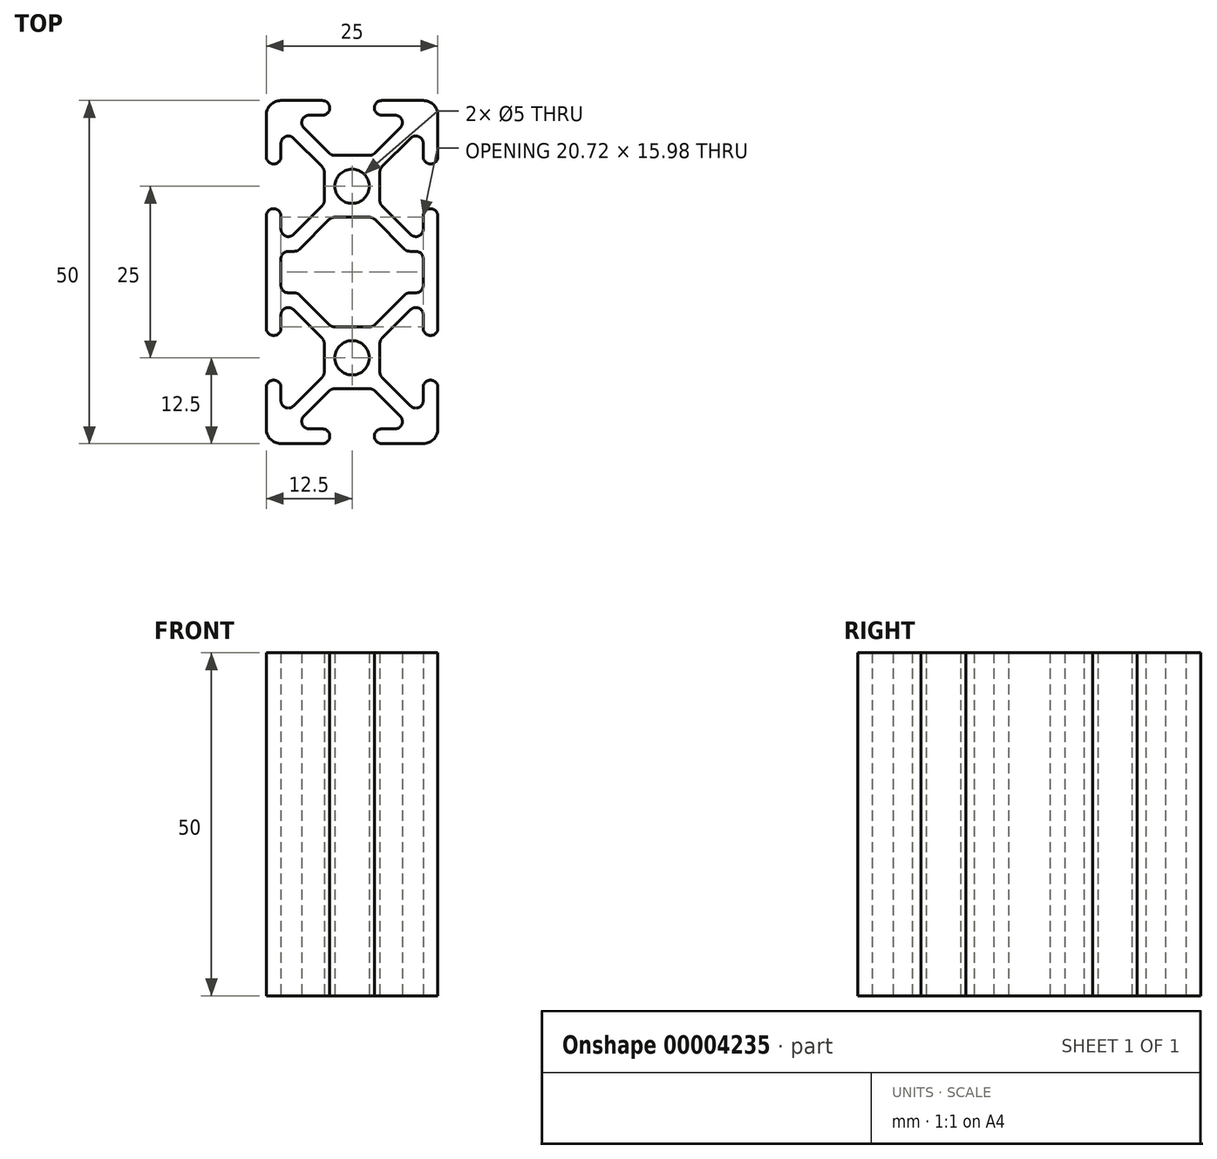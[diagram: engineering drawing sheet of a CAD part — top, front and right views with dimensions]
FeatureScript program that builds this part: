
annotation { "Feature Type Name" : "Feature", "Feature Type Description" : "" }
export const myFeature = defineFeature(function(context is Context, id is Id, definition is map)
    precondition{}
    {
        {
            var Q0;
            Q0=qCreatedBy(makeId("Top.planeOp"),FACE);
            var sketch = newSketch(context, id + "F0", { "sketchPlane" : qUnion([Q0])});
            skCircle(sketch, "E0", {"center": v(0, 0) * mm, "radius": 2.5 * mm});
            skLineSegment(sketch, "E1", {"start": v(0, 0) * mm, "end": v(0, 4.5) * mm, "construction": true});
            skLineSegment(sketch, "E2", {"start": v(0, 0) * mm, "end": v(-4.05, 0) * mm, "construction": true});
            skLineSegment(sketch, "E3", {"start": v(0, 0) * mm, "end": v(-12.5, 12.5) * mm, "construction": true});
            skLineSegment(sketch, "E4", {"start": v(-12.5, 10.36) * mm, "end": v(-12.5, 4.32) * mm});
            skLineSegment(sketch, "E5", {"start": v(-10.36, 12.5) * mm, "end": v(-4.32, 12.5) * mm});
            skLineSegment(sketch, "E6", {"start": v(-4.32, 10.36) * mm, "end": v(-6.26, 10.36) * mm});
            skLineSegment(sketch, "E7", {"start": v(-10.36, 6.26) * mm, "end": v(-10.36, 4.32) * mm});
            skArc(sketch, "E8", {"start": v(-4.32, 12.5) * mm, "mid": v(-3.25, 11.43) * mm, "end": v(-4.32, 10.36) * mm});
            skArc(sketch, "E9", {"start": v(-10.36, 4.32) * mm, "mid": v(-11.43, 3.25) * mm, "end": v(-12.5, 4.32) * mm});
            skLineSegment(sketch, "E10", {"start": v(0, 4.5) * mm, "end": v(-2.55, 4.5) * mm});
            skLineSegment(sketch, "E11", {"start": v(-4.05, 2.1) * mm, "end": v(-4.05, 0) * mm});
            skLineSegment(sketch, "E12", {"start": v(-8.53, 7.02) * mm, "end": v(-4.36, 2.85) * mm});
            skLineSegment(sketch, "E13", {"start": v(-7.02, 8.53) * mm, "end": v(-3.31, 4.82) * mm});
            skLineSegment(sketch, "E14.0.MirrorCS", {"start": v(10.36, 6.26) * mm, "end": v(10.36, 4.32) * mm});
            skLineSegment(sketch, "E14.1.MirrorCS", {"start": v(7.02, 8.53) * mm, "end": v(3.31, 4.82) * mm});
            skArc(sketch, "E14.2.MirrorCS", {"start": v(4.32, 12.5) * mm, "mid": v(3.25, 11.43) * mm, "end": v(4.32, 10.36) * mm});
            skArc(sketch, "E14.3.MirrorCS", {"start": v(10.36, 4.32) * mm, "mid": v(11.43, 3.25) * mm, "end": v(12.5, 4.32) * mm});
            skLineSegment(sketch, "E14.4.MirrorCS", {"start": v(10.36, 12.5) * mm, "end": v(4.32, 12.5) * mm});
            skLineSegment(sketch, "E14.5.MirrorCS", {"start": v(4.32, 10.36) * mm, "end": v(6.26, 10.36) * mm});
            skLineSegment(sketch, "E14.6.MirrorCS", {"start": v(12.5, 10.36) * mm, "end": v(12.5, 4.32) * mm});
            skLineSegment(sketch, "E14.7.MirrorCS", {"start": v(8.53, 7.02) * mm, "end": v(4.36, 2.85) * mm});
            skLineSegment(sketch, "E15.0.MirrorCS", {"start": v(0, 4.5) * mm, "end": v(2.55, 4.5) * mm});
            skLineSegment(sketch, "E16.0.MirrorCS", {"start": v(4.05, 2.1) * mm, "end": v(4.05, 0) * mm});
            skLineSegment(sketch, "E17.1.MirrorCS", {"start": v(12.5, -12.5) * mm, "end": v(12.5, -4.32) * mm});
            skLineSegment(sketch, "E17.5.MirrorCS", {"start": v(10.36, -6.26) * mm, "end": v(10.36, -4.32) * mm});
            skLineSegment(sketch, "E17.6.MirrorCS", {"start": v(8.53, -7.02) * mm, "end": v(4.36, -2.85) * mm});
            skArc(sketch, "E17.10.MirrorCS", {"start": v(10.36, -4.32) * mm, "mid": v(11.43, -3.25) * mm, "end": v(12.5, -4.32) * mm});
            skLineSegment(sketch, "E17.11.MirrorCS", {"start": v(-12.5, -12.5) * mm, "end": v(-12.5, -4.32) * mm});
            skLineSegment(sketch, "E17.14.MirrorCS", {"start": v(-8.53, -7.02) * mm, "end": v(-4.36, -2.85) * mm});
            skArc(sketch, "E17.15.MirrorCS", {"start": v(-10.36, -4.32) * mm, "mid": v(-11.43, -3.25) * mm, "end": v(-12.5, -4.32) * mm});
            skLineSegment(sketch, "E17.16.MirrorCS", {"start": v(-10.36, -6.26) * mm, "end": v(-10.36, -4.32) * mm});
            skLineSegment(sketch, "E18.0.MirrorCS", {"start": v(4.05, -2.1) * mm, "end": v(4.05, 0) * mm});
            skLineSegment(sketch, "E19.0.MirrorCS", {"start": v(-4.05, -2.1) * mm, "end": v(-4.05, 0) * mm});
            skPoint(sketch, "E20.visualSharp", {"position": v(-12.5, 12.5) * mm});
            skArc(sketch, "E20.filletArc", {"start": v(-10.36, 12.5) * mm, "mid": v(-11.87, 11.87) * mm, "end": v(-12.5, 10.36) * mm});
            skPoint(sketch, "E21.visualSharp", {"position": v(12.5, 12.5) * mm});
            skArc(sketch, "E21.filletArc", {"start": v(12.5, 10.36) * mm, "mid": v(11.87, 11.87) * mm, "end": v(10.36, 12.5) * mm});
            skPoint(sketch, "E22.visualSharp", {"position": v(-12.5, -12.5) * mm});
            skPoint(sketch, "E23.visualSharp", {"position": v(4.05, 4.5) * mm});
            skPoint(sketch, "E24.visualSharp", {"position": v(-10.36, 8.85) * mm});
            skArc(sketch, "E24.filletArc", {"start": v(-8.53, 7.02) * mm, "mid": v(-9.7, 7.25) * mm, "end": v(-10.36, 6.26) * mm});
            skPoint(sketch, "E25.visualSharp", {"position": v(-8.85, 10.36) * mm});
            skArc(sketch, "E25.filletArc", {"start": v(-6.26, 10.36) * mm, "mid": v(-7.25, 9.7) * mm, "end": v(-7.02, 8.53) * mm});
            skPoint(sketch, "E26.visualSharp", {"position": v(8.85, 10.36) * mm});
            skArc(sketch, "E26.filletArc", {"start": v(7.02, 8.53) * mm, "mid": v(7.25, 9.7) * mm, "end": v(6.26, 10.36) * mm});
            skArc(sketch, "E27.filletArc", {"start": v(10.36, 6.26) * mm, "mid": v(9.7, 7.25) * mm, "end": v(8.53, 7.02) * mm});
            skArc(sketch, "E28.filletArc", {"start": v(8.53, -7.02) * mm, "mid": v(9.7, -7.25) * mm, "end": v(10.36, -6.26) * mm});
            skArc(sketch, "E29.filletArc", {"start": v(-10.36, -6.26) * mm, "mid": v(-9.7, -7.25) * mm, "end": v(-8.53, -7.02) * mm});
            skPoint(sketch, "E30.orphan", {"position": v(-4.05, 4.5) * mm});
            skPoint(sketch, "E31.visualSharp", {"position": v(-3, 4.5) * mm});
            skArc(sketch, "E31.filletArc", {"start": v(-3.31, 4.82) * mm, "mid": v(-2.96, 4.6) * mm, "end": v(-2.55, 4.5) * mm});
            skPoint(sketch, "E32.visualSharp", {"position": v(3, 4.5) * mm});
            skArc(sketch, "E32.filletArc", {"start": v(2.55, 4.5) * mm, "mid": v(2.96, 4.6) * mm, "end": v(3.31, 4.82) * mm});
            skPoint(sketch, "E33.visualSharp", {"position": v(-4.05, 2.54) * mm});
            skArc(sketch, "E33.filletArc", {"start": v(-4.05, 2.1) * mm, "mid": v(-4.13, 2.5) * mm, "end": v(-4.36, 2.85) * mm});
            skPoint(sketch, "E34.visualSharp", {"position": v(-4.05, -2.54) * mm});
            skArc(sketch, "E34.filletArc", {"start": v(-4.36, -2.85) * mm, "mid": v(-4.13, -2.5) * mm, "end": v(-4.05, -2.1) * mm});
            skPoint(sketch, "E35.visualSharp", {"position": v(4.05, -2.54) * mm});
            skArc(sketch, "E35.filletArc", {"start": v(4.05, -2.1) * mm, "mid": v(4.13, -2.5) * mm, "end": v(4.36, -2.85) * mm});
            skPoint(sketch, "E36.visualSharp", {"position": v(4.05, 2.54) * mm});
            skArc(sketch, "E36.filletArc", {"start": v(4.36, 2.85) * mm, "mid": v(4.13, 2.5) * mm, "end": v(4.05, 2.1) * mm});
            skCircle(sketch, "E37", {"center": v(0, -25) * mm, "radius": 2.5 * mm});
            skLineSegment(sketch, "E38", {"start": v(0, 0) * mm, "end": v(0, -25) * mm, "construction": true});
            skLineSegment(sketch, "E39", {"start": v(0, -12.5) * mm, "end": v(3.65, -12.5) * mm, "construction": true});
            skArc(sketch, "E40.0.MirrorCS", {"start": v(2.55, -29.51) * mm, "mid": v(2.96, -29.6) * mm, "end": v(3.31, -29.82) * mm});
            skArc(sketch, "E40.1.MirrorCS", {"start": v(4.36, -27.85) * mm, "mid": v(4.13, -27.5) * mm, "end": v(4.05, -27.1) * mm});
            skArc(sketch, "E40.2.MirrorCS", {"start": v(-4.05, -27.1) * mm, "mid": v(-4.13, -27.5) * mm, "end": v(-4.36, -27.85) * mm});
            skArc(sketch, "E40.3.MirrorCS", {"start": v(-4.36, -22.15) * mm, "mid": v(-4.13, -22.5) * mm, "end": v(-4.05, -22.9) * mm});
            skArc(sketch, "E40.4.MirrorCS", {"start": v(-3.31, -29.82) * mm, "mid": v(-2.96, -29.6) * mm, "end": v(-2.55, -29.51) * mm});
            skArc(sketch, "E40.5.MirrorCS", {"start": v(4.05, -22.9) * mm, "mid": v(4.13, -22.5) * mm, "end": v(4.36, -22.15) * mm});
            skPoint(sketch, "E40.6.MirrorP", {"position": v(-4.05, -27.54) * mm});
            skPoint(sketch, "E40.7.MirrorP", {"position": v(-10.36, -33.85) * mm});
            skPoint(sketch, "E40.8.MirrorP", {"position": v(4.05, -27.54) * mm});
            skLineSegment(sketch, "E40.10.MirrorCS", {"start": v(0, -25) * mm, "end": v(0, -29.51) * mm, "construction": true});
            skLineSegment(sketch, "E40.11.MirrorCS", {"start": v(-12.5, -35.36) * mm, "end": v(-12.5, -29.32) * mm});
            skLineSegment(sketch, "E40.12.MirrorCS", {"start": v(0, -25) * mm, "end": v(-12.5, -37.5) * mm, "construction": true});
            skLineSegment(sketch, "E40.13.MirrorCS", {"start": v(-4.32, -35.36) * mm, "end": v(-6.26, -35.36) * mm});
            skLineSegment(sketch, "E40.14.MirrorCS", {"start": v(-10.36, -31.26) * mm, "end": v(-10.36, -29.32) * mm});
            skLineSegment(sketch, "E40.15.MirrorCS", {"start": v(0, -29.51) * mm, "end": v(-2.55, -29.51) * mm});
            skPoint(sketch, "E40.16.MirrorP", {"position": v(10.36, -33.85) * mm});
            skLineSegment(sketch, "E40.17.MirrorCS", {"start": v(-4.05, -22.9) * mm, "end": v(-4.05, -25) * mm});
            skLineSegment(sketch, "E40.18.MirrorCS", {"start": v(-8.53, -32.02) * mm, "end": v(-4.36, -27.85) * mm});
            skArc(sketch, "E40.19.MirrorCS", {"start": v(10.36, -29.32) * mm, "mid": v(11.43, -28.25) * mm, "end": v(12.5, -29.32) * mm});
            skArc(sketch, "E40.20.MirrorCS", {"start": v(8.53, -17.98) * mm, "mid": v(9.7, -17.75) * mm, "end": v(10.36, -18.74) * mm});
            skLineSegment(sketch, "E40.21.MirrorCS", {"start": v(-4.05, -27.1) * mm, "end": v(-4.05, -25) * mm});
            skLineSegment(sketch, "E40.22.MirrorCS", {"start": v(12.5, -12.5) * mm, "end": v(12.5, -20.68) * mm});
            skLineSegment(sketch, "E40.23.MirrorCS", {"start": v(8.53, -32.02) * mm, "end": v(4.36, -27.85) * mm});
            skPoint(sketch, "E40.24.MirrorP", {"position": v(-8.85, -35.36) * mm});
            skArc(sketch, "E40.25.MirrorCS", {"start": v(-6.26, -35.36) * mm, "mid": v(-7.25, -34.7) * mm, "end": v(-7.02, -33.53) * mm});
            skArc(sketch, "E40.26.MirrorCS", {"start": v(10.36, -20.68) * mm, "mid": v(11.43, -21.75) * mm, "end": v(12.5, -20.68) * mm});
            skPoint(sketch, "E40.28.MirrorP", {"position": v(-3, -29.51) * mm});
            skLineSegment(sketch, "E40.29.MirrorCS", {"start": v(10.36, -31.26) * mm, "end": v(10.36, -29.32) * mm});
            skLineSegment(sketch, "E40.30.MirrorCS", {"start": v(7.02, -33.53) * mm, "end": v(3.31, -29.82) * mm});
            skPoint(sketch, "E40.31.MirrorP", {"position": v(12.5, -37.5) * mm});
            skLineSegment(sketch, "E40.32.MirrorCS", {"start": v(-10.36, -18.74) * mm, "end": v(-10.36, -20.68) * mm});
            skArc(sketch, "E40.33.MirrorCS", {"start": v(12.5, -35.36) * mm, "mid": v(11.87, -36.87) * mm, "end": v(10.36, -37.5) * mm});
            skArc(sketch, "E40.35.MirrorCS", {"start": v(-10.36, -37.5) * mm, "mid": v(-11.87, -36.87) * mm, "end": v(-12.5, -35.36) * mm});
            skPoint(sketch, "E40.37.MirrorP", {"position": v(-4.05, -22.46) * mm});
            skPoint(sketch, "E40.38.MirrorP", {"position": v(8.85, -35.36) * mm});
            skArc(sketch, "E40.39.MirrorCS", {"start": v(10.36, -31.26) * mm, "mid": v(9.7, -32.25) * mm, "end": v(8.53, -32.02) * mm});
            skLineSegment(sketch, "E40.40.MirrorCS", {"start": v(-8.53, -17.98) * mm, "end": v(-4.36, -22.15) * mm});
            skLineSegment(sketch, "E40.42.MirrorCS", {"start": v(8.53, -17.98) * mm, "end": v(4.36, -22.15) * mm});
            skLineSegment(sketch, "E40.43.MirrorCS", {"start": v(4.05, -22.9) * mm, "end": v(4.05, -25) * mm});
            skArc(sketch, "E40.44.MirrorCS", {"start": v(4.32, -37.5) * mm, "mid": v(3.25, -36.43) * mm, "end": v(4.32, -35.36) * mm});
            skArc(sketch, "E40.45.MirrorCS", {"start": v(-10.36, -18.74) * mm, "mid": v(-9.7, -17.75) * mm, "end": v(-8.53, -17.98) * mm});
            skLineSegment(sketch, "E40.46.MirrorCS", {"start": v(10.36, -18.74) * mm, "end": v(10.36, -20.68) * mm});
            skPoint(sketch, "E40.47.MirrorP", {"position": v(3, -29.51) * mm});
            skPoint(sketch, "E40.48.MirrorP", {"position": v(-4.05, -29.51) * mm});
            skLineSegment(sketch, "E40.49.MirrorCS", {"start": v(0, -29.51) * mm, "end": v(2.55, -29.51) * mm});
            skArc(sketch, "E40.51.MirrorCS", {"start": v(7.02, -33.53) * mm, "mid": v(7.25, -34.7) * mm, "end": v(6.26, -35.36) * mm});
            skPoint(sketch, "E40.52.MirrorP", {"position": v(-12.5, -37.5) * mm});
            skArc(sketch, "E40.53.MirrorCS", {"start": v(-10.36, -20.68) * mm, "mid": v(-11.43, -21.75) * mm, "end": v(-12.5, -20.68) * mm});
            skLineSegment(sketch, "E40.54.MirrorCS", {"start": v(0, -25) * mm, "end": v(-4.05, -25) * mm, "construction": true});
            skLineSegment(sketch, "E40.55.MirrorCS", {"start": v(-10.36, -37.5) * mm, "end": v(-4.32, -37.5) * mm});
            skArc(sketch, "E40.56.MirrorCS", {"start": v(-4.32, -37.5) * mm, "mid": v(-3.25, -36.43) * mm, "end": v(-4.32, -35.36) * mm});
            skArc(sketch, "E40.57.MirrorCS", {"start": v(-10.36, -29.32) * mm, "mid": v(-11.43, -28.25) * mm, "end": v(-12.5, -29.32) * mm});
            skPoint(sketch, "E40.58.MirrorP", {"position": v(4.05, -29.51) * mm});
            skLineSegment(sketch, "E40.59.MirrorCS", {"start": v(-7.02, -33.53) * mm, "end": v(-3.31, -29.82) * mm});
            skLineSegment(sketch, "E40.60.MirrorCS", {"start": v(10.36, -37.5) * mm, "end": v(4.32, -37.5) * mm});
            skLineSegment(sketch, "E40.61.MirrorCS", {"start": v(4.05, -27.1) * mm, "end": v(4.05, -25) * mm});
            skPoint(sketch, "E40.62.MirrorP", {"position": v(4.05, -22.46) * mm});
            skArc(sketch, "E40.63.MirrorCS", {"start": v(-8.53, -32.02) * mm, "mid": v(-9.7, -32.25) * mm, "end": v(-10.36, -31.26) * mm});
            skLineSegment(sketch, "E40.64.MirrorCS", {"start": v(12.5, -35.36) * mm, "end": v(12.5, -29.32) * mm});
            skLineSegment(sketch, "E40.65.MirrorCS", {"start": v(-12.5, -12.5) * mm, "end": v(-12.5, -20.68) * mm});
            skLineSegment(sketch, "E40.67.MirrorCS", {"start": v(4.32, -35.36) * mm, "end": v(6.26, -35.36) * mm});
            skLineSegment(sketch, "E41.0.MirrorCS", {"start": v(0, -4.5) * mm, "end": v(-2.55, -4.5) * mm});
            skPoint(sketch, "E42.visualSharp", {"position": v(-2.55, -4.5) * mm});
            skLineSegment(sketch, "E43", {"start": v(-10.36, -10.54) * mm, "end": v(-10.36, -12.5) * mm});
            skLineSegment(sketch, "E44", {"start": v(-9.3, -9.47) * mm, "end": v(-8.4, -9.47) * mm});
            skLineSegment(sketch, "E45", {"start": v(-3.31, -4.82) * mm, "end": v(-7.65, -9.16) * mm});
            skPoint(sketch, "E46.visualSharp", {"position": v(-3, -4.5) * mm});
            skArc(sketch, "E46.filletArc", {"start": v(-2.55, -4.5) * mm, "mid": v(-2.96, -4.6) * mm, "end": v(-3.31, -4.82) * mm});
            skPoint(sketch, "E47.visualSharp", {"position": v(-7.96, -9.47) * mm});
            skArc(sketch, "E47.filletArc", {"start": v(-8.4, -9.47) * mm, "mid": v(-8, -9.4) * mm, "end": v(-7.65, -9.16) * mm});
            skPoint(sketch, "E48.visualSharp", {"position": v(-10.36, -9.47) * mm});
            skArc(sketch, "E48.filletArc", {"start": v(-9.3, -9.47) * mm, "mid": v(-10.05, -9.79) * mm, "end": v(-10.36, -10.54) * mm});
            skLineSegment(sketch, "E49.0.MirrorCS", {"start": v(0, -4.5) * mm, "end": v(2.55, -4.5) * mm});
            skArc(sketch, "E50.0.MirrorCS", {"start": v(2.55, -4.5) * mm, "mid": v(2.96, -4.6) * mm, "end": v(3.31, -4.82) * mm});
            skLineSegment(sketch, "E51.0.MirrorCS", {"start": v(3.31, -4.82) * mm, "end": v(7.65, -9.16) * mm});
            skPoint(sketch, "E52.0.MirrorP", {"position": v(7.96, -9.47) * mm});
            skArc(sketch, "E53.0.MirrorCS", {"start": v(8.4, -9.47) * mm, "mid": v(8, -9.4) * mm, "end": v(7.65, -9.16) * mm});
            skLineSegment(sketch, "E54.0.MirrorCS", {"start": v(9.3, -9.47) * mm, "end": v(8.4, -9.47) * mm});
            skArc(sketch, "E55.0.MirrorCS", {"start": v(9.3, -9.47) * mm, "mid": v(10.05, -9.79) * mm, "end": v(10.36, -10.54) * mm});
            skLineSegment(sketch, "E56.0.MirrorCS", {"start": v(10.36, -10.54) * mm, "end": v(10.36, -12.5) * mm});
            skLineSegment(sketch, "E57.0.MirrorCS", {"start": v(10.36, -14.46) * mm, "end": v(10.36, -12.5) * mm});
            skArc(sketch, "E58.0.MirrorCS", {"start": v(9.3, -15.53) * mm, "mid": v(10.05, -15.21) * mm, "end": v(10.36, -14.46) * mm});
            skLineSegment(sketch, "E59.0.MirrorCS", {"start": v(9.3, -15.53) * mm, "end": v(8.4, -15.53) * mm});
            skArc(sketch, "E60.0.MirrorCS", {"start": v(8.4, -15.53) * mm, "mid": v(8, -15.6) * mm, "end": v(7.65, -15.84) * mm});
            skLineSegment(sketch, "E61.0.MirrorCS", {"start": v(3.31, -20.18) * mm, "end": v(7.65, -15.84) * mm});
            skArc(sketch, "E62.0.MirrorCS", {"start": v(2.55, -20.5) * mm, "mid": v(2.96, -20.4) * mm, "end": v(3.31, -20.18) * mm});
            skLineSegment(sketch, "E63.0.MirrorCS", {"start": v(0, -20.5) * mm, "end": v(2.55, -20.5) * mm});
            skLineSegment(sketch, "E64.0.MirrorCS", {"start": v(0, -20.5) * mm, "end": v(-2.55, -20.5) * mm});
            skArc(sketch, "E65.0.MirrorCS", {"start": v(-2.55, -20.5) * mm, "mid": v(-2.96, -20.4) * mm, "end": v(-3.31, -20.18) * mm});
            skLineSegment(sketch, "E66.0.MirrorCS", {"start": v(-3.31, -20.18) * mm, "end": v(-7.65, -15.84) * mm});
            skArc(sketch, "E67.0.MirrorCS", {"start": v(-8.4, -15.53) * mm, "mid": v(-8, -15.6) * mm, "end": v(-7.65, -15.84) * mm});
            skLineSegment(sketch, "E68.0.MirrorCS", {"start": v(-9.3, -15.53) * mm, "end": v(-8.4, -15.53) * mm});
            skArc(sketch, "E69.0.MirrorCS", {"start": v(-9.3, -15.53) * mm, "mid": v(-10.05, -15.21) * mm, "end": v(-10.36, -14.46) * mm});
            skLineSegment(sketch, "E70.0.MirrorCS", {"start": v(-10.36, -14.46) * mm, "end": v(-10.36, -12.5) * mm});
            skSolve(sketch);
        }
        {
            var Q0;
            Q0=makeQuery(id+"F0.imprint","IMPRINT",FACE,{"disambiguationData":[TD([[makeQuery(id+"F0.imprint","IMPRINT",EDGE,{"derivedFrom":sQuery(id+"F0.wireOp",EDGE,"E0")}),-1.0]])]});
            extrude(context, id + "F1", {"entities" : qUnion([Q0]), "depth" : 50 * mm});
        }
    });
